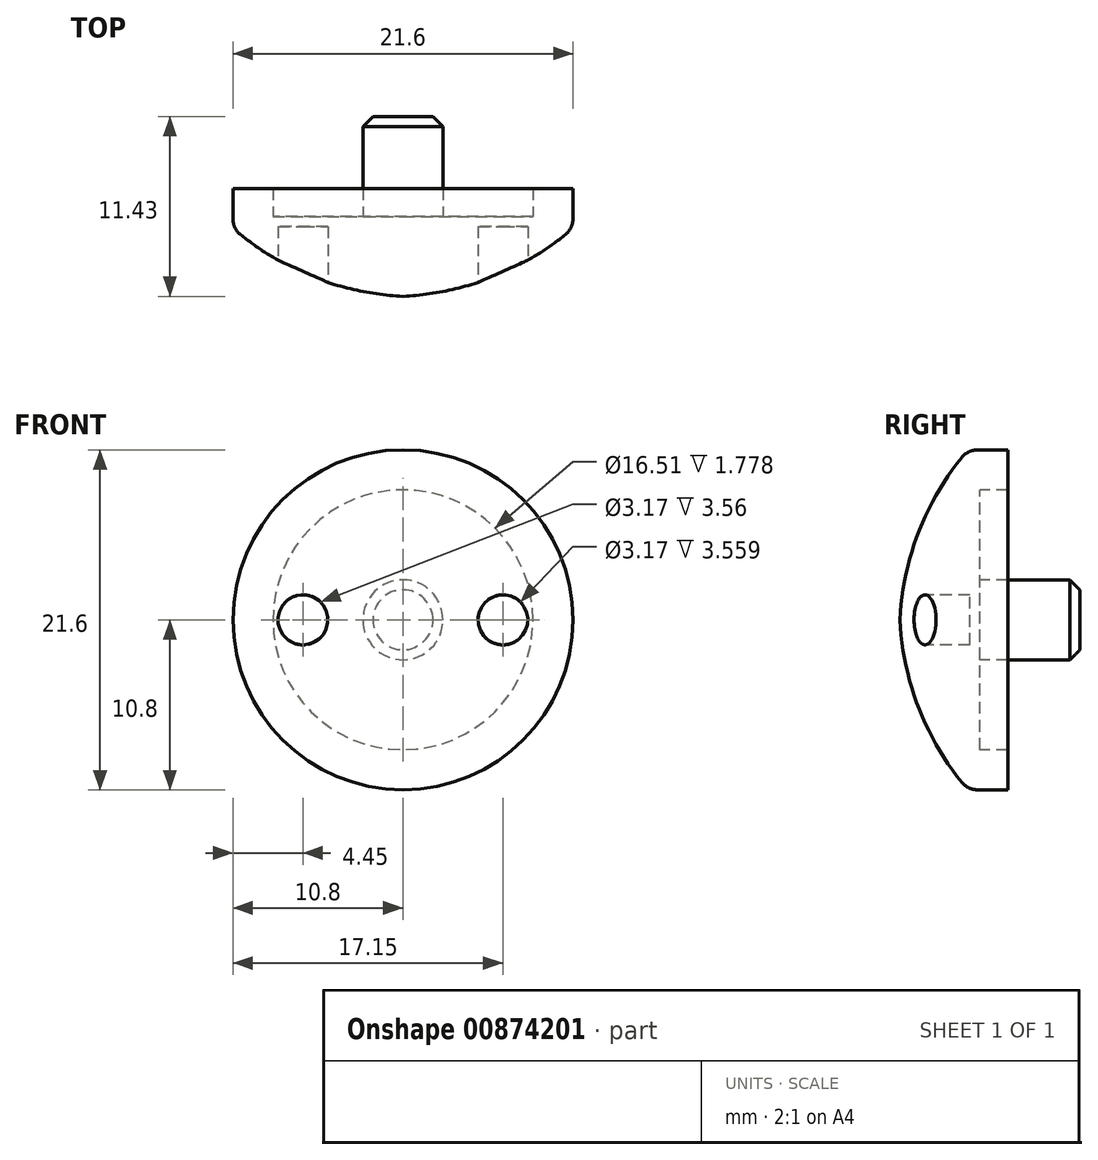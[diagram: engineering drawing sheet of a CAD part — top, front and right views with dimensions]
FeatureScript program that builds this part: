
annotation { "Feature Type Name" : "Feature", "Feature Type Description" : "" }
export const myFeature = defineFeature(function(context is Context, id is Id, definition is map)
    precondition{}
    {
        {
            var Q0;
            Q0=qCreatedBy(makeId("Right.planeOp"),FACE);
            var sketch = newSketch(context, id + "F0", { "sketchPlane" : qUnion([Q0])});
            skLineSegment(sketch, "E0", {"start": v(0, 0) * mm, "end": v(0, 2.54) * mm});
            skLineSegment(sketch, "E1", {"start": v(0, 2.54) * mm, "end": v(-6.35, 2.54) * mm});
            skLineSegment(sketch, "E2", {"start": v(-6.35, 2.54) * mm, "end": v(-6.35, 8.26) * mm});
            skLineSegment(sketch, "E3", {"start": v(-6.35, 8.26) * mm, "end": v(-4.57, 8.26) * mm});
            skLineSegment(sketch, "E4", {"start": v(-4.57, 8.26) * mm, "end": v(-4.57, 10.8) * mm});
            skLineSegment(sketch, "E5", {"start": v(-4.57, 10.8) * mm, "end": v(-7.11, 10.8) * mm});
            skArc(sketch, "E6", {"start": v(-7.11, 10.8) * mm, "mid": v(-10.18, 5.76) * mm, "end": v(-11.43, 0) * mm});
            skLineSegment(sketch, "E7", {"start": v(-11.43, 0) * mm, "end": v(0, 0) * mm});
            skSolve(sketch);
        }
        {
            var Q0;
            Q0=makeQuery(id+"F0.imprint","IMPRINT",FACE,{"disambiguationData":[TD([[makeQuery(id+"F0.imprint","IMPRINT",EDGE,{"derivedFrom":sQuery(id+"F0.wireOp",EDGE,"E0")}),1.0]])]});
            var Q1;
            Q1=sQuery(id+"F0.wireOp",EDGE,"E7");
            revolve(context, id + "F1", {"surfaceOperationType" : NewSurfaceOperationType.NEW, "entities" : qUnion([Q0]), "axis" : qUnion([Q1]), "revolveType" : RevolveType.FULL});
        }
        {
            var Q0;
            Q0=makeQuery(id+"F1.opRevolve","SWEPT_EDGE",EDGE,{"disambiguationData":[OSD([sQuery(id+"F0.wireOp",EDGE,"E5"),sQuery(id+"F0.wireOp",EDGE,"E6")])]});
            fillet(context, id + "F2", {"entities" : qUnion([Q0]), "radius" : 1.27 * mm, "tangentPropagation" : true, "allowEdgeOverflow" : false});
        }
        {
            var Q0;
            Q0=makeQuery(id+"F1.opRevolve","SWEPT_EDGE",EDGE,{"disambiguationData":[OSD([sQuery(id+"F0.wireOp",EDGE,"E0"),sQuery(id+"F0.wireOp",EDGE,"E1")])]});
            chamfer(context, id + "F3", {"entities" : qUnion([Q0]), "width" : 0.64 * mm, "tangentPropagation" : true});
        }
        {
            var Q0;
            Q0=qCreatedBy(makeId("Front.planeOp"),FACE);
            cPlane(context, id + "F4", {"entities" : qUnion([Q0]), "cplaneType" : CPlaneType.OFFSET, "offset" : 11.43 * mm, "width" : 152.4 * mm, "height" : 152.4 * mm});
        }
        {
            var Q0;
            Q0=qCreatedBy(id+"F4.planeOp",FACE);
            var sketch = newSketch(context, id + "F5", { "sketchPlane" : qUnion([Q0])});
            skCircle(sketch, "E8", {"center": v(6.35, 0) * mm, "radius": 1.59 * mm});
            skCircle(sketch, "E9", {"center": v(-6.35, 0) * mm, "radius": 1.59 * mm});
            skSolve(sketch);
        }
        {
            var Q0;
            Q0 = qSketchRegion(id + "F5", true);
            extrude(context, id + "F6", {"entities" : qUnion([Q0]), "operationType" : NewBodyOperationType.REMOVE, "oppositeDirection" : true, "depth" : 4.44 * mm, "offsetDistance" : 25.4 * mm});
        }
    });
